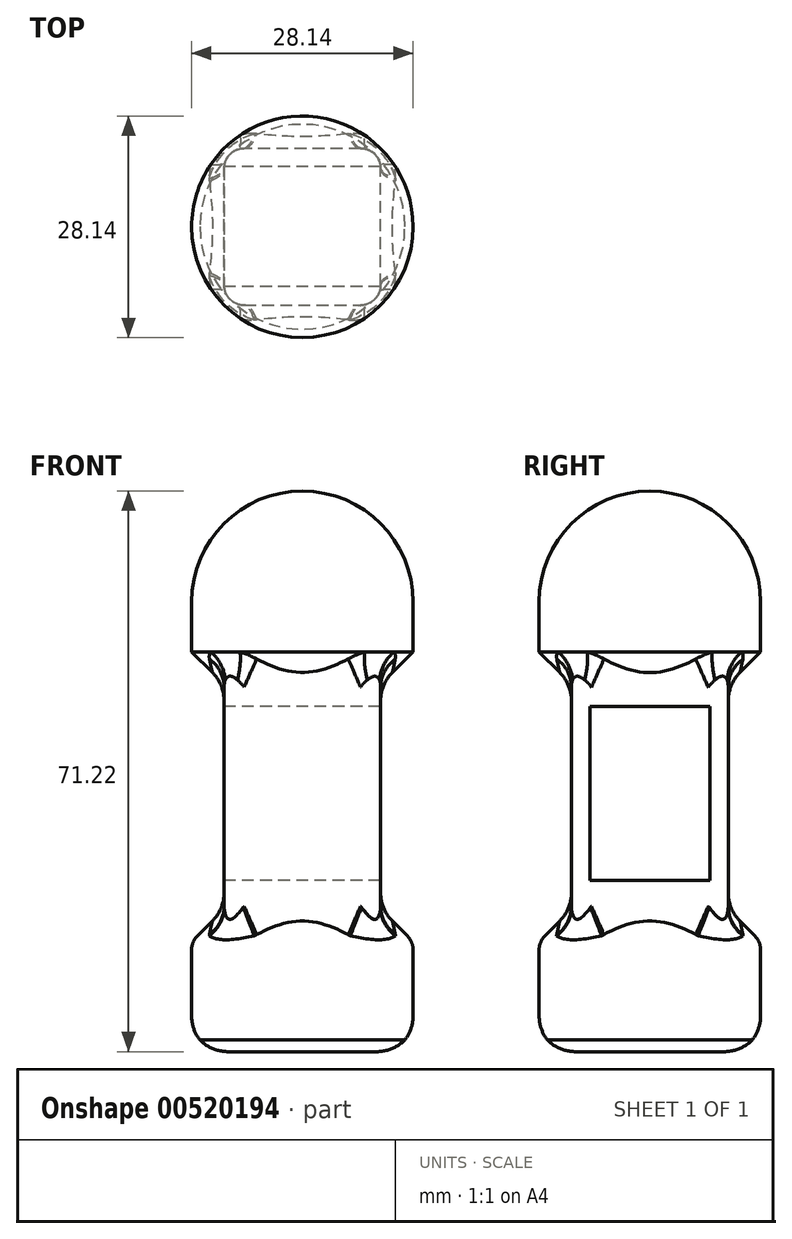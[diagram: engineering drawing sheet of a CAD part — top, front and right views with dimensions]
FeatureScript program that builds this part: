
annotation { "Feature Type Name" : "Feature", "Feature Type Description" : "" }
export const myFeature = defineFeature(function(context is Context, id is Id, definition is map)
    precondition{}
    {
        {
            var Q0;
            Q0=qCreatedBy(makeId("Top.planeOp"),FACE);
            var sketch = newSketch(context, id + "F0", { "sketchPlane" : qUnion([Q0])});
            skCircle(sketch, "E0", {"center": v(0, 0) * mm, "radius": 14.07 * mm});
            skSolve(sketch);
        }
        {
            var Q0;
            Q0=makeQuery(id+"F0.imprint","IMPRINT",FACE,{"disambiguationData":[TD([[makeQuery(id+"F0.imprint","IMPRINT",EDGE,{"derivedFrom":sQuery(id+"F0.wireOp",EDGE,"E0")}),1.0]])]});
            extrude(context, id + "F1", {"entities" : qUnion([Q0]), "depth" : 19.05 * mm, "offsetDistance" : 25.4 * mm});
        }
        {
            var Q0;
            Q0=makeQuery(id+"F1.opExtrude","CAP_FACE",FACE,{"disambiguationData":[OSD([sQuery(id+"F0.wireOp",EDGE,"E0")])],"isStart":false});
            var sketch = newSketch(context, id + "F2", { "sketchPlane" : qUnion([Q0])});
            skLineSegment(sketch, "E1.bottom", {"start": v(9.94, -9.96) * mm, "end": v(-9.94, -9.96) * mm});
            skLineSegment(sketch, "E1.top", {"start": v(9.94, 9.96) * mm, "end": v(-9.94, 9.96) * mm});
            skLineSegment(sketch, "E1.left", {"start": v(9.94, -9.96) * mm, "end": v(9.94, 9.96) * mm});
            skLineSegment(sketch, "E1.right", {"start": v(-9.94, -9.96) * mm, "end": v(-9.94, 9.96) * mm});
            skPoint(sketch, "E1.middle", {"position": v(0, 0) * mm});
            skSolve(sketch);
        }
        {
            var Q0;
            Q0=makeQuery(id+"F2.imprint","IMPRINT",FACE,{"disambiguationData":[TD([[makeQuery(id+"F2.imprint","IMPRINT",EDGE,{"derivedFrom":sQuery(id+"F2.wireOp",EDGE,"E1.bottom")}),-1.0]])]});
            extrude(context, id + "F3", {"entities" : qUnion([Q0]), "operationType" : NewBodyOperationType.ADD, "depth" : 26.67 * mm, "offsetDistance" : 25.4 * mm});
        }
        {
            var Q0;
            Q0=makeQuery(id+"F3.opExtrude","CAP_FACE",FACE,{"disambiguationData":[OSD([sQuery(id+"F2.wireOp",EDGE,"E1.bottom"),sQuery(id+"F2.wireOp",EDGE,"E1.top"),sQuery(id+"F2.wireOp",EDGE,"E1.left"),sQuery(id+"F2.wireOp",EDGE,"E1.right")])],"isStart":false});
            var sketch = newSketch(context, id + "F4", { "sketchPlane" : qUnion([Q0])});
            skCircle(sketch, "E2", {"center": v(0, 0) * mm, "radius": 14.07 * mm});
            skSolve(sketch);
        }
        {
            var Q0;
            Q0 = qSketchRegion(id + "F4", true);
            extrude(context, id + "F5", {"entities" : qUnion([Q0]), "operationType" : NewBodyOperationType.ADD, "depth" : 11.43 * mm, "offsetDistance" : 25.4 * mm});
        }
        {
            var Q0;
            Q0=makeQuery(id+"F5.opExtrude","CAP_FACE",FACE,{"disambiguationData":[OSD([sQuery(id+"F4.wireOp",EDGE,"E2")])],"isStart":false});
            var sketch = newSketch(context, id + "F6", { "sketchPlane" : qUnion([Q0])});
            skLineSegment(sketch, "E3", {"start": v(-14.07, 0) * mm, "end": v(14.07, 0) * mm});
            skSolve(sketch);
        }
        {
            var Q0;
            {var subQ0=sQuery(id+"F6.wireOp",EDGE,"E3");Q0=makeQuery(id+"F6.imprint","IMPRINT",FACE,{"disambiguationData":[TD([[makeQuery(id+"F6.imprint","IMPRINT",EDGE,{"derivedFrom":subQ0}),-1.0]])]});}
            var Q1;
            Q1=sQuery(id+"F6.wireOp",EDGE,"E3");
            revolve(context, id + "F7", {"operationType" : NewBodyOperationType.ADD, "entities" : qUnion([Q0]), "axis" : qUnion([Q1]), "revolveType" : RevolveType.FULL});
        }
        {
            var Q0;
            Q0=makeQuery(id+"F3.opExtrude","SWEPT_FACE",FACE,{"disambiguationData":[OSD([sQuery(id+"F2.wireOp",EDGE,"E1.right")])]});
            var sketch = newSketch(context, id + "F8", { "sketchPlane" : qUnion([Q0])});
            skLineSegment(sketch, "E4.bottom", {"start": v(7.62, 21.78) * mm, "end": v(-7.62, 21.78) * mm});
            skLineSegment(sketch, "E4.top", {"start": v(7.62, 43.88) * mm, "end": v(-7.62, 43.88) * mm});
            skLineSegment(sketch, "E4.left", {"start": v(7.62, 21.78) * mm, "end": v(7.62, 43.88) * mm});
            skLineSegment(sketch, "E4.right", {"start": v(-7.62, 21.78) * mm, "end": v(-7.62, 43.88) * mm});
            skPoint(sketch, "E4.middle", {"position": v(0, 32.83) * mm});
            skSolve(sketch);
        }
        {
            var Q0;
            Q0 = qSketchRegion(id + "F8", true);
            extrude(context, id + "F9", {"entities" : qUnion([Q0]), "operationType" : NewBodyOperationType.REMOVE, "oppositeDirection" : true, "depth" : 25.4 * mm, "offsetDistance" : 25.4 * mm});
        }
        {
            var Q0;
            Q0=makeQuery(id+"F1.opExtrude","CAP_EDGE",EDGE,{"disambiguationData":[OSD([sQuery(id+"F0.wireOp",EDGE,"E0")])],"isStart":true});
            chamfer(context, id + "F10", {"entities" : qUnion([Q0]), "width" : 2.54 * mm, "tangentPropagation" : true});
        }
        {
            var Q0;
            {var subQ0=sQuery(id+"F0.wireOp",EDGE,"E0");Q0=makeQuery(id+"F10.opChamfer","BLEND_EDGE",EDGE,{"blendedFrom":[makeQuery(id+"F1.opExtrude","CAP_EDGE",EDGE,{"disambiguationData":[OSD([subQ0])],"isStart":true}),makeQuery(id+"F1.opExtrude","CAP_FACE",FACE,{"disambiguationData":[OSD([subQ0])],"isStart":true})],"blendedInto":[makeQuery(id+"F1.opExtrude","CAP_FACE",FACE,{"disambiguationData":[OSD([subQ0])],"isStart":true})]});}
            fillet(context, id + "F11", {"entities" : qUnion([Q0]), "radius" : 5.08 * mm, "tangentPropagation" : true, "allowEdgeOverflow" : false});
        }
        {
            var Q0;
            {var subQ0=sQuery(id+"F0.wireOp",EDGE,"E0");Q0=makeQuery(id+"F10.opChamfer","BLEND_EDGE",EDGE,{"blendedFrom":[makeQuery(id+"F1.opExtrude","CAP_EDGE",EDGE,{"disambiguationData":[OSD([subQ0])],"isStart":true}),makeQuery(id+"F1.opExtrude","SWEPT_FACE",FACE,{"disambiguationData":[OSD([subQ0])]})],"blendedInto":[makeQuery(id+"F1.opExtrude","SWEPT_FACE",FACE,{"disambiguationData":[OSD([subQ0])]})]});}
            fillet(context, id + "F12", {"entities" : qUnion([Q0]), "radius" : 5.08 * mm, "tangentPropagation" : true, "allowEdgeOverflow" : false});
        }
        {
            var Q0;
            Q0=makeQuery(id+"F3.opExtrude","SWEPT_EDGE",EDGE,{"disambiguationData":[OSD([sQuery(id+"F0.wireOp",EDGE,"E0"),sQuery(id+"F2.wireOp",EDGE,"E1.bottom"),sQuery(id+"F2.wireOp",EDGE,"E1.left")])]});
            var Q1;
            Q1=makeQuery(id+"F3.opExtrude","SWEPT_EDGE",EDGE,{"disambiguationData":[OSD([sQuery(id+"F0.wireOp",EDGE,"E0"),sQuery(id+"F2.wireOp",EDGE,"E1.top"),sQuery(id+"F2.wireOp",EDGE,"E1.left")])]});
            var Q2;
            Q2=makeQuery(id+"F3.opExtrude","SWEPT_EDGE",EDGE,{"disambiguationData":[OSD([sQuery(id+"F0.wireOp",EDGE,"E0"),sQuery(id+"F2.wireOp",EDGE,"E1.top"),sQuery(id+"F2.wireOp",EDGE,"E1.right")])]});
            var Q3;
            Q3=makeQuery(id+"F3.opExtrude","SWEPT_EDGE",EDGE,{"disambiguationData":[OSD([sQuery(id+"F0.wireOp",EDGE,"E0"),sQuery(id+"F2.wireOp",EDGE,"E1.bottom"),sQuery(id+"F2.wireOp",EDGE,"E1.right")])]});
            fillet(context, id + "F13", {"entities" : qUnion([Q0, Q1, Q2, Q3]), "radius" : 2.54 * mm, "tangentPropagation" : true, "allowEdgeOverflow" : false});
        }
        {
            var Q0;
            {var subQ0=sQuery(id+"F0.wireOp",EDGE,"E0");Q0=makeQuery(id+"F3.boolean.opBoolean","SPLIT",EDGE,{"disambiguationData":[TD([makeQuery(id+"F1.opExtrude","SWEPT_FACE",FACE,{"disambiguationData":[OSD([subQ0])]}),makeQuery(id+"F1.opExtrude","CAP_FACE",FACE,{"disambiguationData":[OSD([subQ0])],"isStart":false}),makeQuery(id+"F3.opExtrude","SWEPT_FACE",FACE,{"disambiguationData":[OSD([sQuery(id+"F2.wireOp",EDGE,"E1.bottom")])]}),makeQuery(id+"F3.opExtrude","SWEPT_FACE",FACE,{"disambiguationData":[OSD([sQuery(id+"F2.wireOp",EDGE,"E1.left")])]}),makeQuery(id+"F3.opExtrude","SWEPT_FACE",FACE,{"disambiguationData":[OSD([sQuery(id+"F2.wireOp",EDGE,"E1.right")])]})])],"derivedFrom":makeQuery(id+"F1.opExtrude","CAP_EDGE",EDGE,{"disambiguationData":[OSD([subQ0])],"isStart":false})});}
            chamfer(context, id + "F14", {"entities" : qUnion([Q0]), "width" : 5.08 * mm, "tangentPropagation" : true});
        }
        {
            var Q0;
            {var subQ0=sQuery(id+"F4.wireOp",EDGE,"E2");Q0=makeQuery(id+"F5.boolean.opBoolean","SPLIT",EDGE,{"disambiguationData":[TD([makeQuery(id+"F3.opExtrude","SWEPT_FACE",FACE,{"disambiguationData":[OSD([sQuery(id+"F2.wireOp",EDGE,"E1.bottom")])]}),makeQuery(id+"F3.opExtrude","SWEPT_FACE",FACE,{"disambiguationData":[OSD([sQuery(id+"F2.wireOp",EDGE,"E1.top")])]}),makeQuery(id+"F3.opExtrude","SWEPT_FACE",FACE,{"disambiguationData":[OSD([sQuery(id+"F2.wireOp",EDGE,"E1.left")])]}),makeQuery(id+"F5.opExtrude","SWEPT_FACE",FACE,{"disambiguationData":[OSD([subQ0])]}),makeQuery(id+"F5.opExtrude","CAP_FACE",FACE,{"disambiguationData":[OSD([subQ0])],"isStart":true})])],"derivedFrom":makeQuery(id+"F5.opExtrude","CAP_EDGE",EDGE,{"disambiguationData":[OSD([subQ0])],"isStart":true})});}
            chamfer(context, id + "F15", {"entities" : qUnion([Q0]), "width" : 5.08 * mm, "tangentPropagation" : true});
        }
        {
            var Q0;
            {var subQ0=sQuery(id+"F4.wireOp",EDGE,"E2");var subQ1=makeQuery(id+"F5.opExtrude","SWEPT_FACE",FACE,{"disambiguationData":[OSD([subQ0])]});Q0=makeQuery(id+"F15.opChamfer","BLEND_EDGE",EDGE,{"blendedFrom":[makeQuery(id+"F5.boolean.opBoolean","SPLIT",EDGE,{"disambiguationData":[TD([makeQuery(id+"F3.opExtrude","SWEPT_FACE",FACE,{"disambiguationData":[OSD([sQuery(id+"F2.wireOp",EDGE,"E1.bottom")])]}),makeQuery(id+"F3.opExtrude","SWEPT_FACE",FACE,{"disambiguationData":[OSD([sQuery(id+"F2.wireOp",EDGE,"E1.top")])]}),makeQuery(id+"F3.opExtrude","SWEPT_FACE",FACE,{"disambiguationData":[OSD([sQuery(id+"F2.wireOp",EDGE,"E1.left")])]}),subQ1,makeQuery(id+"F5.opExtrude","CAP_FACE",FACE,{"disambiguationData":[OSD([subQ0])],"isStart":true})])],"derivedFrom":makeQuery(id+"F5.opExtrude","CAP_EDGE",EDGE,{"disambiguationData":[OSD([subQ0])],"isStart":true})}),subQ1],"blendedInto":[subQ1]});}
            var Q1;
            {var subQ0=sQuery(id+"F0.wireOp",EDGE,"E0");var subQ1=makeQuery(id+"F1.opExtrude","SWEPT_FACE",FACE,{"disambiguationData":[OSD([subQ0])]});Q1=makeQuery(id+"F14.opChamfer","BLEND_EDGE",EDGE,{"blendedFrom":[makeQuery(id+"F3.boolean.opBoolean","SPLIT",EDGE,{"disambiguationData":[TD([subQ1,makeQuery(id+"F1.opExtrude","CAP_FACE",FACE,{"disambiguationData":[OSD([subQ0])],"isStart":false}),makeQuery(id+"F3.opExtrude","SWEPT_FACE",FACE,{"disambiguationData":[OSD([sQuery(id+"F2.wireOp",EDGE,"E1.bottom")])]}),makeQuery(id+"F3.opExtrude","SWEPT_FACE",FACE,{"disambiguationData":[OSD([sQuery(id+"F2.wireOp",EDGE,"E1.left")])]}),makeQuery(id+"F3.opExtrude","SWEPT_FACE",FACE,{"disambiguationData":[OSD([sQuery(id+"F2.wireOp",EDGE,"E1.right")])]})])],"derivedFrom":makeQuery(id+"F1.opExtrude","CAP_EDGE",EDGE,{"disambiguationData":[OSD([subQ0])],"isStart":false})}),subQ1],"blendedInto":[subQ1]});}
            fillet(context, id + "F16", {"entities" : qUnion([Q0, Q1]), "radius" : 2.54 * mm, "tangentPropagation" : true, "allowEdgeOverflow" : false});
        }
        {
            var Q0;
            {var subQ0=makeQuery(id+"F3.opExtrude","SWEPT_FACE",FACE,{"disambiguationData":[OSD([sQuery(id+"F2.wireOp",EDGE,"E1.bottom")])]});var subQ1=sQuery(id+"F4.wireOp",EDGE,"E2");Q0=makeQuery(id+"F15.opChamfer","BLEND_EDGE",EDGE,{"blendedFrom":[makeQuery(id+"F5.boolean.opBoolean","SPLIT",EDGE,{"disambiguationData":[TD([subQ0,makeQuery(id+"F3.opExtrude","SWEPT_FACE",FACE,{"disambiguationData":[OSD([sQuery(id+"F2.wireOp",EDGE,"E1.left")])]}),makeQuery(id+"F3.opExtrude","SWEPT_FACE",FACE,{"disambiguationData":[OSD([sQuery(id+"F2.wireOp",EDGE,"E1.right")])]}),makeQuery(id+"F5.opExtrude","SWEPT_FACE",FACE,{"disambiguationData":[OSD([subQ1])]}),makeQuery(id+"F5.opExtrude","CAP_FACE",FACE,{"disambiguationData":[OSD([subQ1])],"isStart":true})])],"derivedFrom":makeQuery(id+"F5.opExtrude","CAP_EDGE",EDGE,{"disambiguationData":[OSD([subQ1])],"isStart":true})}),subQ0],"blendedInto":[subQ0]});}
            var Q1;
            {var subQ0=makeQuery(id+"F3.opExtrude","SWEPT_FACE",FACE,{"disambiguationData":[OSD([sQuery(id+"F2.wireOp",EDGE,"E1.right")])]});var subQ1=sQuery(id+"F0.wireOp",EDGE,"E0");Q1=makeQuery(id+"F14.opChamfer","BLEND_EDGE",EDGE,{"blendedFrom":[makeQuery(id+"F3.boolean.opBoolean","SPLIT",EDGE,{"disambiguationData":[TD([makeQuery(id+"F1.opExtrude","SWEPT_FACE",FACE,{"disambiguationData":[OSD([subQ1])]}),makeQuery(id+"F1.opExtrude","CAP_FACE",FACE,{"disambiguationData":[OSD([subQ1])],"isStart":false}),makeQuery(id+"F3.opExtrude","SWEPT_FACE",FACE,{"disambiguationData":[OSD([sQuery(id+"F2.wireOp",EDGE,"E1.bottom")])]}),makeQuery(id+"F3.opExtrude","SWEPT_FACE",FACE,{"disambiguationData":[OSD([sQuery(id+"F2.wireOp",EDGE,"E1.top")])]}),subQ0])],"derivedFrom":makeQuery(id+"F1.opExtrude","CAP_EDGE",EDGE,{"disambiguationData":[OSD([subQ1])],"isStart":false})}),makeQuery(id+"F13.opFillet","SPLIT",FACE,{"disambiguationData":[OD(0.0)],"derivedFrom":subQ0})],"blendedInto":[makeQuery(id+"F13.opFillet","SPLIT",FACE,{"disambiguationData":[OD(0.0)],"derivedFrom":subQ0})]});}
            fillet(context, id + "F17", {"entities" : qUnion([Q0, Q1]), "radius" : 5.08 * mm, "tangentPropagation" : true, "allowEdgeOverflow" : false});
        }
        {
            var Q0;
            Q0=makeQuery(id+"F1.opExtrude","SWEPT_BODY",BODY,{"disambiguationData":[OSD([sQuery(id+"F0.wireOp",EDGE,"E0")])]});
            transform(context, id + "F18", {"entities" : qUnion([Q0]), "transformType" : TransformType.TRANSLATION_3D, "dx" : 0 * mm, "dy" : 0 * mm, "dz" : -33.02 * mm, "makeCopy" : false});
        }
    });
